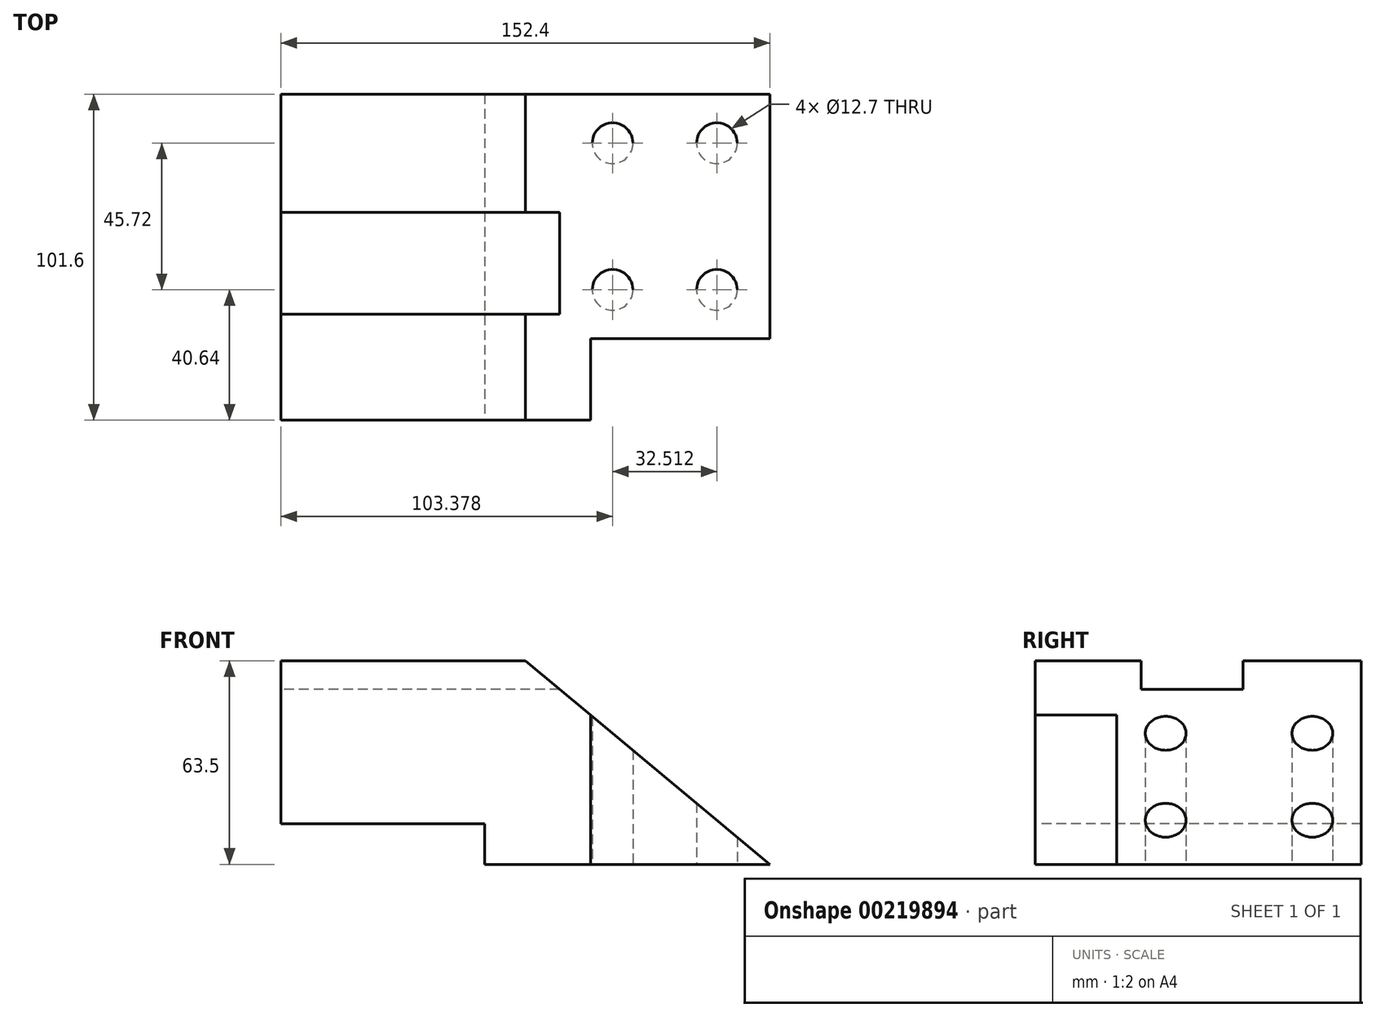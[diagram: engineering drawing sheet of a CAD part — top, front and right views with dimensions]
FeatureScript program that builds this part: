
annotation { "Feature Type Name" : "Feature", "Feature Type Description" : "" }
export const myFeature = defineFeature(function(context is Context, id is Id, definition is map)
    precondition{}
    {
        {
            var Q0;
            Q0=qCreatedBy(makeId("Right.planeOp"),FACE);
            var sketch = newSketch(context, id + "F0", { "sketchPlane" : qUnion([Q0])});
            skLineSegment(sketch, "E0.bottom", {"start": v(-50.8, 31.75) * mm, "end": v(-17.78, 31.75) * mm});
            skLineSegment(sketch, "E0.top", {"start": v(-50.8, -31.75) * mm, "end": v(50.8, -31.75) * mm});
            skLineSegment(sketch, "E0.left", {"start": v(-50.8, 31.75) * mm, "end": v(-50.8, -31.75) * mm});
            skLineSegment(sketch, "E0.right", {"start": v(50.8, 31.75) * mm, "end": v(50.8, -31.75) * mm});
            skPoint(sketch, "E0.middle", {"position": v(0, 0) * mm});
            skLineSegment(sketch, "E1.top", {"start": v(-17.78, 22.86) * mm, "end": v(13.97, 22.86) * mm});
            skLineSegment(sketch, "E1.left", {"start": v(-17.78, 31.75) * mm, "end": v(-17.78, 22.86) * mm});
            skLineSegment(sketch, "E1.right", {"start": v(13.97, 31.75) * mm, "end": v(13.97, 22.86) * mm});
            skLineSegment(sketch, "E2.trimOffspring", {"start": v(13.97, 31.75) * mm, "end": v(50.8, 31.75) * mm});
            skSolve(sketch);
        }
        {
            var Q0;
            Q0 = qSketchRegion(id + "F0", true);
            extrude(context, id + "F1", {"entities" : qUnion([Q0]), "depth" : 152.4 * mm});
        }
        {
            var Q0;
            Q0=makeQuery(id+"F1.opExtrude","SWEPT_FACE",FACE,{"disambiguationData":[OSD([sQuery(id+"F0.wireOp",EDGE,"E0.left")])]});
            var sketch = newSketch(context, id + "F2", { "sketchPlane" : qUnion([Q0])});
            skLineSegment(sketch, "E3.bottom", {"start": v(0, -31.75) * mm, "end": v(63.5, -31.75) * mm});
            skLineSegment(sketch, "E3.top", {"start": v(0, -19.05) * mm, "end": v(63.5, -19.05) * mm});
            skLineSegment(sketch, "E3.left", {"start": v(0, -31.75) * mm, "end": v(0, -19.05) * mm});
            skLineSegment(sketch, "E3.right", {"start": v(63.5, -31.75) * mm, "end": v(63.5, -19.05) * mm});
            skLineSegment(sketch, "E4.bottom", {"start": v(96.52, 26.67) * mm, "end": v(152.4, 26.67) * mm});
            skLineSegment(sketch, "E4.top", {"start": v(96.52, -31.75) * mm, "end": v(152.4, -31.75) * mm});
            skLineSegment(sketch, "E4.left", {"start": v(96.52, 26.67) * mm, "end": v(96.52, -31.75) * mm});
            skLineSegment(sketch, "E4.right", {"start": v(152.4, 26.67) * mm, "end": v(152.4, -31.75) * mm});
            skSolve(sketch);
        }
        {
            var Q0;
            Q0=makeQuery(id+"F2.imprint","IMPRINT",FACE,{"disambiguationData":[TD([[makeQuery(id+"F2.imprint","IMPRINT",EDGE,{"derivedFrom":sQuery(id+"F2.wireOp",EDGE,"E3.bottom")}),-1.0]])]});
            extrude(context, id + "F3", {"entities" : qUnion([Q0]), "operationType" : NewBodyOperationType.REMOVE, "endBound" : BoundingType.THROUGH_ALL, "oppositeDirection" : true, "depth" : 25.4 * mm});
        }
        {
            var Q0;
            Q0=makeQuery(id+"F2.imprint","IMPRINT",FACE,{"disambiguationData":[TD([[makeQuery(id+"F2.imprint","IMPRINT",EDGE,{"derivedFrom":sQuery(id+"F2.wireOp",EDGE,"E4.bottom")}),-1.0]])]});
            extrude(context, id + "F4", {"entities" : qUnion([Q0]), "operationType" : NewBodyOperationType.REMOVE, "oppositeDirection" : true, "depth" : 25.4 * mm});
        }
        {
            var Q0;
            {var subQ5=sQuery(id+"F2.wireOp",EDGE,"E3.top");Q0=makeQuery(id+"F2.imprint","IMPRINT",FACE,{"disambiguationData":[TD([[makeQuery(id+"F2.imprint","IMPRINT",EDGE,{"derivedFrom":subQ5}),1.0]])]});}
            var sketch = newSketch(context, id + "F5", { "sketchPlane" : qUnion([Q0])});
            skLineSegment(sketch, "E5.0", {"start": v(152.4, 31.75) * mm, "end": v(76.2, 31.75) * mm});
            skLineSegment(sketch, "E6.0", {"start": v(152.4, 26.67) * mm, "end": v(152.4, -31.75) * mm});
            skLineSegment(sketch, "E7.0", {"start": v(152.4, 31.75) * mm, "end": v(152.4, 26.67) * mm});
            skLineSegment(sketch, "E8", {"start": v(152.4, -31.75) * mm, "end": v(76.2, 31.75) * mm});
            skPoint(sketch, "E9.orphan", {"position": v(0, 31.75) * mm});
            skSolve(sketch);
        }
        {
            var Q0;
            Q0 = qSketchRegion(id + "F5", true);
            extrude(context, id + "F6", {"entities" : qUnion([Q0]), "operationType" : NewBodyOperationType.REMOVE, "endBound" : BoundingType.THROUGH_ALL, "oppositeDirection" : true, "depth" : 25.4 * mm});
        }
        {
            var Q0;
            Q0=makeQuery(id+"F1.opExtrude","SWEPT_FACE",FACE,{"disambiguationData":[OSD([sQuery(id+"F0.wireOp",EDGE,"E0.top")])]});
            var sketch = newSketch(context, id + "F7", { "sketchPlane" : qUnion([Q0])});
            skLineSegment(sketch, "E10", {"start": v(152.4, 25.4) * mm, "end": v(96.52, -50.8) * mm, "construction": true});
            skLineSegment(sketch, "E11", {"start": v(152.4, -50.8) * mm, "end": v(96.52, 25.4) * mm, "construction": true});
            skLineSegment(sketch, "E12", {"start": v(152.4, -12.7) * mm, "end": v(96.52, -12.7) * mm, "construction": true});
            skLineSegment(sketch, "E13", {"start": v(96.52, 25.4) * mm, "end": v(96.52, -50.8) * mm, "construction": true});
            skCircle(sketch, "E14", {"center": v(103.38, 10.16) * mm, "radius": 6.35 * mm});
            skCircle(sketch, "E15", {"center": v(135.9, 10.16) * mm, "radius": 6.35 * mm});
            skLineSegment(sketch, "E16.0", {"start": v(152.4, 15.78) * mm, "end": v(96.52, 15.78) * mm});
            skCircle(sketch, "E17.MirrorC", {"center": v(135.9, -35.56) * mm, "radius": 6.35 * mm});
            skCircle(sketch, "E18.MirrorC", {"center": v(103.38, -35.56) * mm, "radius": 6.35 * mm});
            skSolve(sketch);
        }
        {
            var Q0;
            Q0 = qSketchRegion(id + "F7", true);
            extrude(context, id + "F8", {"entities" : qUnion([Q0]), "operationType" : NewBodyOperationType.REMOVE, "endBound" : BoundingType.THROUGH_ALL, "oppositeDirection" : true, "depth" : 25.4 * mm});
        }
    });
